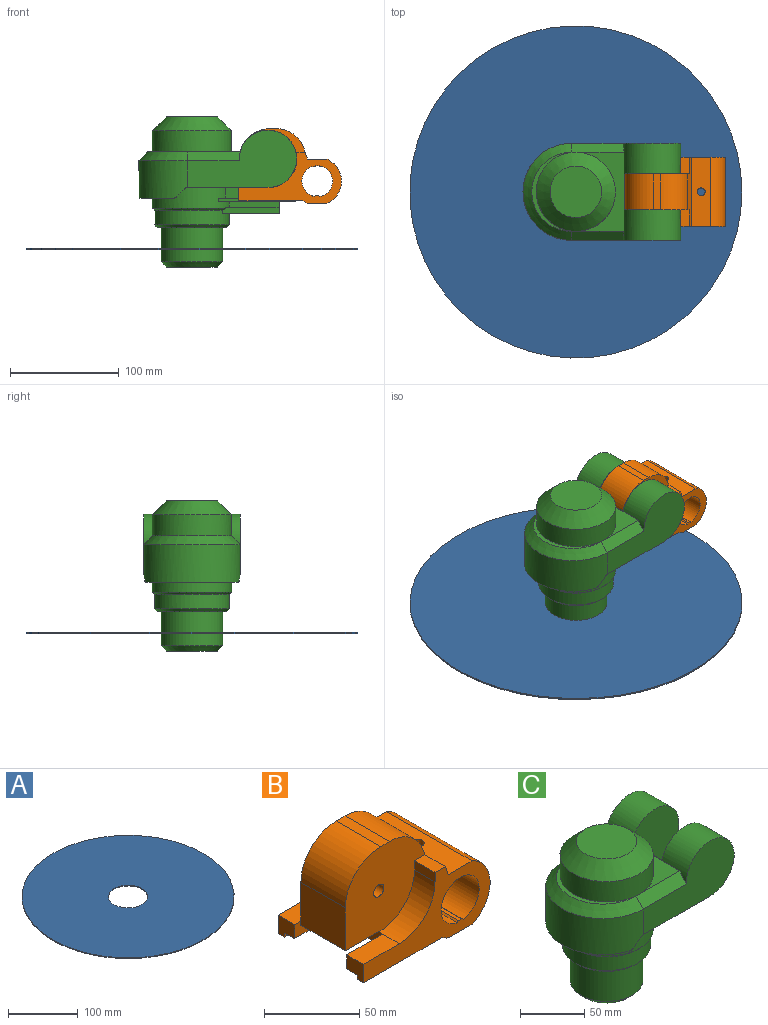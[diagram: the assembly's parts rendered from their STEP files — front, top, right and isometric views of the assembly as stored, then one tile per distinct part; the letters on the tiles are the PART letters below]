
ASSEMBLY  parts=3 mates=4
PART A: 4 faces, bbox 304.8x304.8x1.3 mm
  f0: cylinder r=28.26mm len=56.52mm, axis (0,0,-1), area 225.5mm2, adj f2,f3
  f1: cylinder r=152.4mm len=304.8mm, axis (0,0,-1), area 1216.1mm2, adj f2,f3
  f2: plane 304.8x304.8mm, normal (0,0,1), area 70457.4mm2, adj f0,f1
  f3: plane 304.8x304.8mm, normal (0,0,-1), area 70457.4mm2, adj f0,f1
PART B: 43 faces, bbox 94.1x63.5x68.7 mm
  f0: plane 28.98x1.09mm, normal (-0.62,0,0.78), area 38.7mm2, adj f1,f11,f23,f41
  f1: plane 28.37x2.29mm, normal (0,0,1), area 64.6mm2, adj f0,f11,f22,f41
  f2: plane 28.98x1.09mm, normal (0.62,0,0.78), area 38.7mm2, adj f3,f21,f23,f41
  f3: plane 94.11x47.06mm, normal (0,-1,0), area 1710.4mm2, adj f2,f4,f9,f20,f21,f23,f26,f27
  f4: plane 63.5x58.55mm, normal (0,0,-1), area 880.8mm2, adj f3,f9,f11,f13,f16,f30,f31,f38
  f5: plane 15.24x7.62mm, normal (0,0,1), area 116.1mm2, adj f6,f11,f15,f35
  f6: plane 15.24x6.03mm, normal (-1,0,0), area 91.9mm2, adj f5,f11,f15,f24
  f7: plane 26.67x8.88mm, normal (0,-1,0), area 236.7mm2, adj f8,f13,f25,f29
  f8: plane 38.61x9.13mm, normal (-1,0,0), area 325.8mm2, adj f7,f10,f14,f15,f17,f24,f27,f29
  f9: plane 12.45x11.87mm, normal (-1,0,0), area 126.1mm2, adj f3,f4,f10,f28,f31,f32
  f10: plane 26.67x8.88mm, normal (0,1,0), area 236.7mm2, adj f8,f9,f28,f32
  f11: plane 94.11x47.06mm, normal (0,1,0), area 1710.4mm2, adj f0,f1,f4,f5,f6,f13,f22,f23
  f12: plane 33.02x6.55mm, normal (0,0,1), area 216.2mm2, adj f14,f15,f19,f40
  f13: plane 12.45x11.87mm, normal (-1,0,0), area 126.1mm2, adj f4,f7,f11,f25,f29,f30
  f14: plane 59.06x54.17mm, normal (0,-1,0), area 2453.4mm2, adj f8,f12,f17,f18,f19,f26,f27,f33
  f15: plane 59.06x54.17mm, normal (0,1,0), area 2453.4mm2, adj f5,f6,f8,f12,f17,f18,f19,f24
  f16: plane 54.48x4.31mm, normal (-1,0,0), area 184.3mm2, adj f4,f29,f30,f31,f32
  f17: plane 33.02x24.89mm, normal (0,0,-1), area 821.9mm2, adj f8,f14,f15,f18
  f18: plane 33.02x27.62mm, normal (-1,0,0), area 912.1mm2, adj f14,f15,f17,f19
  f19: cylinder r=26.29mm len=33.02mm, axis (0,-1,0), area 1363.5mm2, adj f12,f14,f15,f18
  f20: plane 28.98x1.09mm, normal (-0.62,0,0.78), area 38.7mm2, adj f3,f21,f23,f41
  f21: plane 28.37x2.29mm, normal (0,0,1), area 64.6mm2, adj f2,f3,f20,f41
  f22: plane 28.98x1.09mm, normal (0.62,0,0.78), area 38.7mm2, adj f1,f11,f23,f41
  f23: cylinder r=14.13mm len=63.5mm, axis (0,-1,0), area 5305.5mm2, adj f0,f2,f3,f11,f20,f22,f41,f42
  f24: cylinder r=26.54mm len=26.54mm, axis (0,1,0), area 635.4mm2, adj f6,f8,f11,f15,f25
  f25: plane 26.67x12.45mm, normal (0,0,1), area 331.9mm2, adj f7,f11,f13,f24
  f26: plane 15.24x6.03mm, normal (-1,0,0), area 91.9mm2, adj f3,f14,f27,f34
  f27: cylinder r=26.54mm len=26.54mm, axis (0,-1,0), area 635.4mm2, adj f3,f8,f14,f26,f28
  f28: plane 26.67x12.45mm, normal (0,0,1), area 331.9mm2, adj f3,f9,f10,f27
  f29: plane 52.07x27.24mm, normal (0,-0.07,-1), area 905.7mm2, adj f7,f8,f13,f16,f30,f32
  f30: plane 52.07x2.46mm, normal (0,-1,0), area 128.1mm2, adj f4,f13,f16,f29
  f31: plane 52.07x2.46mm, normal (0,1,0), area 128.1mm2, adj f4,f9,f16,f32
  f32: plane 52.07x27.24mm, normal (0,0.07,-1), area 905.7mm2, adj f8,f9,f10,f16,f29,f31
  f33: cylinder r=3.81mm len=33.02mm, axis (0,1,0), area 790.5mm2, adj f14,f15
  f34: plane 15.24x7.62mm, normal (0,0,1), area 116.1mm2, adj f3,f14,f26,f35
  f35: plane 63.5x10.33mm, normal (0.94,0,0.33), area 564.5mm2, adj f3,f5,f11,f14,f15,f34,f37,f40
  f36: cylinder r=22.23mm len=63.5mm, axis (0,1,0), area 3279.9mm2, adj f3,f11,f37,f39
  f37: plane 63.5x17.67mm, normal (0,0,1), area 1081.9mm2, adj f3,f11,f35,f36,f42
  f38: cylinder r=22.23mm len=63.5mm, axis (0,1,0), area 331.3mm2, adj f3,f4,f11,f39
  f39: plane 63.5x17.67mm, normal (0,0,-1), area 1081.9mm2, adj f3,f11,f36,f38,f41
  f40: cylinder r=26.29mm len=33.02mm, axis (0,1,0), area 1069mm2, adj f12,f14,f15,f35
  f41: cylinder r=3.57mm len=7.28mm, axis (0,0,1), area 152.6mm2, adj f0,f1,f2,f20,f21,f22,f23,f39
  f42: cylinder r=3.57mm len=7.14mm, axis (0,0,1), area 145.6mm2, adj f23,f37
PART C: 52 faces, bbox 144.8x89x137.9 mm
  f0: cylinder r=34.29mm len=68.58mm, axis (0,0,-1), area 2720.2mm2, adj f2,f6,f21,f22,f24
  f1: cylinder r=36.32mm len=72.64mm, axis (0,0,-1), area 2698.7mm2, adj f2,f8,f9,f11,f12,f13,f14,f15
  f2: cone r=36.32mm half-angle=45deg, axis (0,0,1), area 519.6mm2, adj f0,f1,f21,f22
  f3: cylinder r=28.26mm len=56.52mm, axis (0,0,-1), area 5524.4mm2, adj f5,f7
  f4: plane 46.36x46.36mm, normal (0,0,-1), area 1687.7mm2, adj f7
  f5: plane 63.5x63.5mm, normal (0,0,-1), area 658.4mm2, adj f3,f6
  f6: cone r=34.29mm half-angle=45deg, axis (0,0,1), area 745.3mm2, adj f0,f5
  f7: cone r=28.26mm half-angle=45deg, axis (0,0,1), area 1160.9mm2, adj f3,f4
  f8: plane 39.08x9.39mm, normal (0,1,0), area 366.8mm2, adj f1,f9,f23,f46
  f9: plane 73.33x25.15mm, normal (0,0,-1), area 1415.4mm2, adj f1,f8,f16,f31,f33
  f10: plane 72.64x44.34mm, normal (0,0,1), area 1148.7mm2, adj f31,f38,f40,f51
  f11: plane 45.49x5.27mm, normal (0,-1,0), area 239.8mm2, adj f1,f25,f26,f28
  f12: plane 45.49x5.84mm, normal (0,1,0), area 265.8mm2, adj f1,f25,f27,f28
  f13: plane 10.94x7.04mm, normal (0.71,0,-0.71), area 90.5mm2, adj f1,f15,f16,f36
  f14: cylinder r=5.08mm len=11.55mm, axis (0,-1,0), area 40.5mm2, adj f1,f35,f36,f37
  f15: cylinder r=5.08mm len=11.55mm, axis (0,-1,0), area 40.5mm2, adj f1,f13,f35,f36
  f16: cylinder r=5.08mm len=8.82mm, axis (0,1,0), area 34mm2, adj f1,f9,f13,f33,f36
  f17: cylinder r=5.08mm len=8.82mm, axis (0,1,0), area 34mm2, adj f1,f30,f32,f36,f37
  f18: plane 70.94x3.18mm, normal (0,1,0), area 225.2mm2, adj f1,f28,f29,f46
  f19: plane 70.94x3.18mm, normal (0,-1,0), area 225.2mm2, adj f1,f28,f29,f45,f48
  f20: plane 39.08x9.91mm, normal (0,-1,0), area 387.2mm2, adj f1,f23,f32,f47,f48
  f21: plane 51.76x5.31mm, normal (0,1,0), area 269.6mm2, adj f0,f1,f2,f24,f25,f27
  f22: plane 51.76x5.89mm, normal (0,-1,0), area 297.8mm2, adj f0,f1,f2,f24,f25,f26
  f23: plane 38.61x9.39mm, normal (1,0,0), area 337.1mm2, adj f8,f20,f31,f42,f45,f46
  f24: plane 51.71x38.74mm, normal (0,0,-1), area 1845.4mm2, adj f0,f21,f22,f25
  f25: plane 38.74x11.11mm, normal (1,0,0), area 340.8mm2, adj f11,f12,f21,f22,f24,f26,f27,f28
  f26: plane 49.28x8.06mm, normal (0,0,1), area 380.5mm2, adj f1,f11,f22,f25
  f27: plane 49.28x8.06mm, normal (0,0,1), area 380.5mm2, adj f1,f12,f21,f25
  f28: plane 70.94x53.98mm, normal (0,0,-1), area 2379mm2, adj f1,f11,f12,f18,f19,f25,f29
  f29: plane 53.98x5mm, normal (1,0,0), area 220.7mm2, adj f18,f19,f28,f45,f46
  f30: plane 100.2x52.61mm, normal (0,-1,0), area 3486.8mm2, adj f17,f31,f32,f36,f38
  f31: cylinder r=26.29mm len=88.9mm, axis (0,-1,0), area 6645.5mm2, adj f9,f10,f23,f30,f32,f33,f38,f40
  f32: plane 73.33x25.15mm, normal (0,0,-1), area 1415.4mm2, adj f1,f17,f20,f30,f31
  f33: plane 100.2x52.61mm, normal (0,1,0), area 3486.8mm2, adj f9,f16,f31,f36,f40
  f34: plane 72.64x40.39mm, normal (0,0,1), area 295.2mm2, adj f38,f39,f40,f51
  f35: plane 84.68x30.92mm, normal (0,0,-1), area 1073.4mm2, adj f1,f14,f15,f36
  f36: cylinder r=44.45mm len=88.9mm, axis (0,0,1), area 4676.8mm2, adj f13,f14,f15,f16,f17,f30,f33,f35
  f37: plane 10.94x7.04mm, normal (0.71,0,-0.71), area 90.5mm2, adj f1,f14,f17,f36
  f38: plane 48.46x8.19mm, normal (0,-0.71,0.71), area 549.8mm2, adj f10,f30,f31,f34,f39
  f39: cone r=36.32mm half-angle=45deg, axis (0,0,-1), area 1458.4mm2, adj f34,f36,f38,f40
  f40: plane 48.46x8.19mm, normal (0,0.71,0.71), area 549.8mm2, adj f10,f31,f33,f34,f39
  f41: plane 52.58x51.69mm, normal (0,1,0), area 2292.1mm2, adj f31,f42,f44
  f42: plane 33.02x25.4mm, normal (0,0,1), area 838.7mm2, adj f23,f41,f43,f44
  f43: plane 52.58x51.69mm, normal (0,-1,0), area 2292.1mm2, adj f31,f42,f44
  f44: plane 33.07x33.02mm, normal (1,0,0), area 1091.9mm2, adj f31,f41,f42,f43
  f45: plane 26.99x25.4mm, normal (0,-0.07,1), area 687.1mm2, adj f19,f23,f29,f46,f47
  f46: plane 70.97x27.02mm, normal (0,0.07,1), area 1010.6mm2, adj f1,f8,f18,f23,f29,f45
  f47: plane 7.68x0.52mm, normal (-1,0,0), area 2mm2, adj f20,f45,f48
  f48: plane 45.54x7.68mm, normal (0,0,1), area 322.8mm2, adj f1,f19,f20,f47
  f49: plane 47.24x47.24mm, normal (0,0,1), area 1753mm2, adj f50
  f50: cone r=23.62mm half-angle=45deg, axis (0,0,-1), area 3382.3mm2, adj f49,f51
  f51: cylinder r=36.32mm len=72.64mm, axis (0,0,-1), area 4420mm2, adj f10,f34,f50
PLACE A t=(290.68,602.24,175.89)mm
PLACE B t=(290.68,602.24,160.01)mm
PLACE C t=(290.68,602.24,160.01)mm
MATE planar C.f31 <-> B.f14  axis (0,1,0) through (360.53,585.73,259.39)mm
MATE planar B.f16 <-> C.f29  axis (-1,0,0) through (385.93,602.24,222.71)mm
MATE planar C.f3 <-> A.f1  axis (0,0,-1) through (290.68,602.24,160.01)mm
MATE cylindrical C.f3 <-> A.f0  axis (0,0,-1) through (290.68,602.24,180.65)mm
